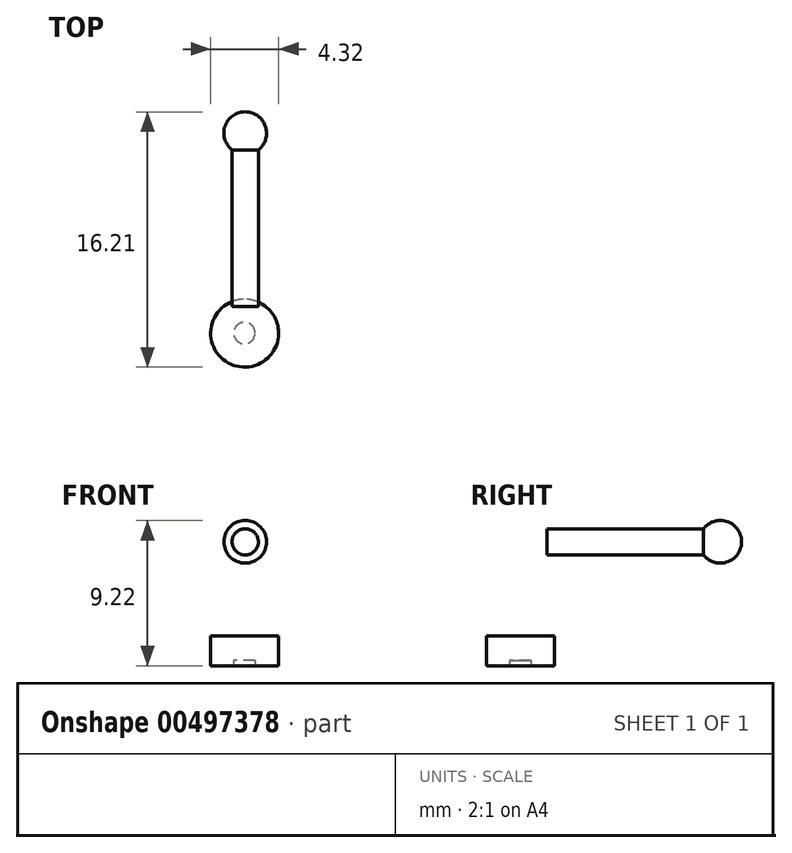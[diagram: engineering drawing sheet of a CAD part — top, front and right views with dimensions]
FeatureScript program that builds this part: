
annotation { "Feature Type Name" : "Feature", "Feature Type Description" : "" }
export const myFeature = defineFeature(function(context is Context, id is Id, definition is map)
    precondition{}
    {
        {
            var Q0;
            Q0=qCreatedBy(makeId("Front.planeOp"),FACE);
            var sketch = newSketch(context, id + "F0", { "sketchPlane" : qUnion([Q0])});
            skCircle(sketch, "E0", {"center": v(-8.94, 7.87) * mm, "radius": 0.83 * mm});
            skSolve(sketch);
        }
        {
            var Q0;
            Q0=makeQuery(id+"F0.imprint","IMPRINT",FACE,{"disambiguationData":[TD([[makeQuery(id+"F0.imprint","IMPRINT",EDGE,{"derivedFrom":sQuery(id+"F0.wireOp",EDGE,"E0")}),1.0]])]});
            extrude(context, id + "F1", {"entities" : qUnion([Q0]), "depth" : 11 * mm});
        }
        {
            var Q0;
            Q0=qCreatedBy(makeId("Front.planeOp"),FACE);
            var sketch = newSketch(context, id + "F2", { "sketchPlane" : qUnion([Q0])});
            skArc(sketch, "E1", {"start": v(-8.95, 6.51) * mm, "mid": v(-7.6, 7.87) * mm, "end": v(-8.95, 9.22) * mm});
            skLineSegment(sketch, "E2", {"start": v(-8.95, 6.51) * mm, "end": v(-8.95, 9.22) * mm});
            skSolve(sketch);
        }
        {
            var Q0;
            Q0=makeQuery(id+"F2.imprint","IMPRINT",FACE,{"disambiguationData":[TD([[makeQuery(id+"F2.imprint","IMPRINT",EDGE,{"derivedFrom":sQuery(id+"F2.wireOp",EDGE,"E1")}),1.0]])]});
            var Q1;
            Q1=sQuery(id+"F2.wireOp",EDGE,"E2");
            revolve(context, id + "F3", {"operationType" : NewBodyOperationType.ADD, "entities" : qUnion([Q0]), "axis" : qUnion([Q1]), "revolveType" : RevolveType.FULL});
        }
        {
            var Q0;
            Q0=qCreatedBy(makeId("Top.planeOp"),FACE);
            var sketch = newSketch(context, id + "F4", { "sketchPlane" : qUnion([Q0])});
            skCircle(sketch, "E3", {"center": v(-8.98, -12.7) * mm, "radius": 2.16 * mm});
            skSolve(sketch);
        }
        {
            var Q0;
            Q0 = qSketchRegion(id + "F4", true);
            extrude(context, id + "F5", {"entities" : qUnion([Q0]), "depth" : 1.9 * mm});
        }
        {
            var Q0;
            Q0=qCreatedBy(makeId("Top.planeOp"),FACE);
            var sketch = newSketch(context, id + "F6", { "sketchPlane" : qUnion([Q0])});
            skCircle(sketch, "E4", {"center": v(-9, -12.7) * mm, "radius": 0.68 * mm});
            skSolve(sketch);
        }
        {
            var Q0;
            Q0=makeQuery(id+"F6.imprint","IMPRINT",FACE,{"disambiguationData":[TD([[makeQuery(id+"F6.imprint","IMPRINT",EDGE,{"derivedFrom":sQuery(id+"F6.wireOp",EDGE,"E4")}),1.0]])]});
            var Q1;
            Q1=sQuery(id+"F6.wireOp",EDGE,"E4");
            extrude(context, id + "F7", {"entities" : qUnion([Q0]), "surfaceEntities" : qUnion([Q1]), "depth" : 0.33 * mm});
        }
    });
